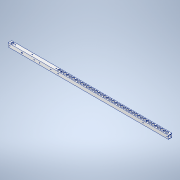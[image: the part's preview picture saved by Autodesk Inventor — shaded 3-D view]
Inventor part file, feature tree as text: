
AUTODESK INVENTOR PART (.ipt)
format: ipt  version: 2020.3 (Build 243373000, 373)  size: 290,304 bytes
history: native  units: mm
features: sketch x12, hole x9, extrude x3, other x1
ambient origin geometry x8: Origin, YZ Plane, XZ Plane, XY Plane, X Axis, Y Axis, Z Axis, Center Point
bodies: Body1 (feature_tree)
feature tree (25):
  other  "ソリッド1"
  extrude  "押し出し1"  Depth=15.0mm
  hole  "穴1"  [1 undecoded]
  hole  "穴2"  [1 undecoded]
  hole  "穴3"  [1 undecoded]
  extrude  "押し出し2"  Depth=1.2mm
  hole  "穴4"  [1 undecoded]
  hole  "穴5"  [1 undecoded]
  hole  "穴6"  [1 undecoded]
  extrude  "押し出し3"  Depth=7.5mm
  hole  "穴8"  [1 undecoded]
  hole  "穴9"  [1 undecoded]
  hole  "穴10"  [1 undecoded]
  sketch  "スケッチ1"
  sketch  "スケッチ2"
  sketch  "スケッチ3"
  sketch  "スケッチ4"
  sketch  "スケッチ5"
  sketch  "スケッチ6"
  sketch  "スケッチ7"
  sketch  "スケッチ8"
  sketch  "スケッチ11"
  sketch  "スケッチ12"
  sketch  "スケッチ13"
  sketch  "スケッチ14"
note: 9 required parameter values undecoded (feature->parameter linkage not recoverable at this tier; creation-order binding heuristic only, values carry confidence <= 0.55)
